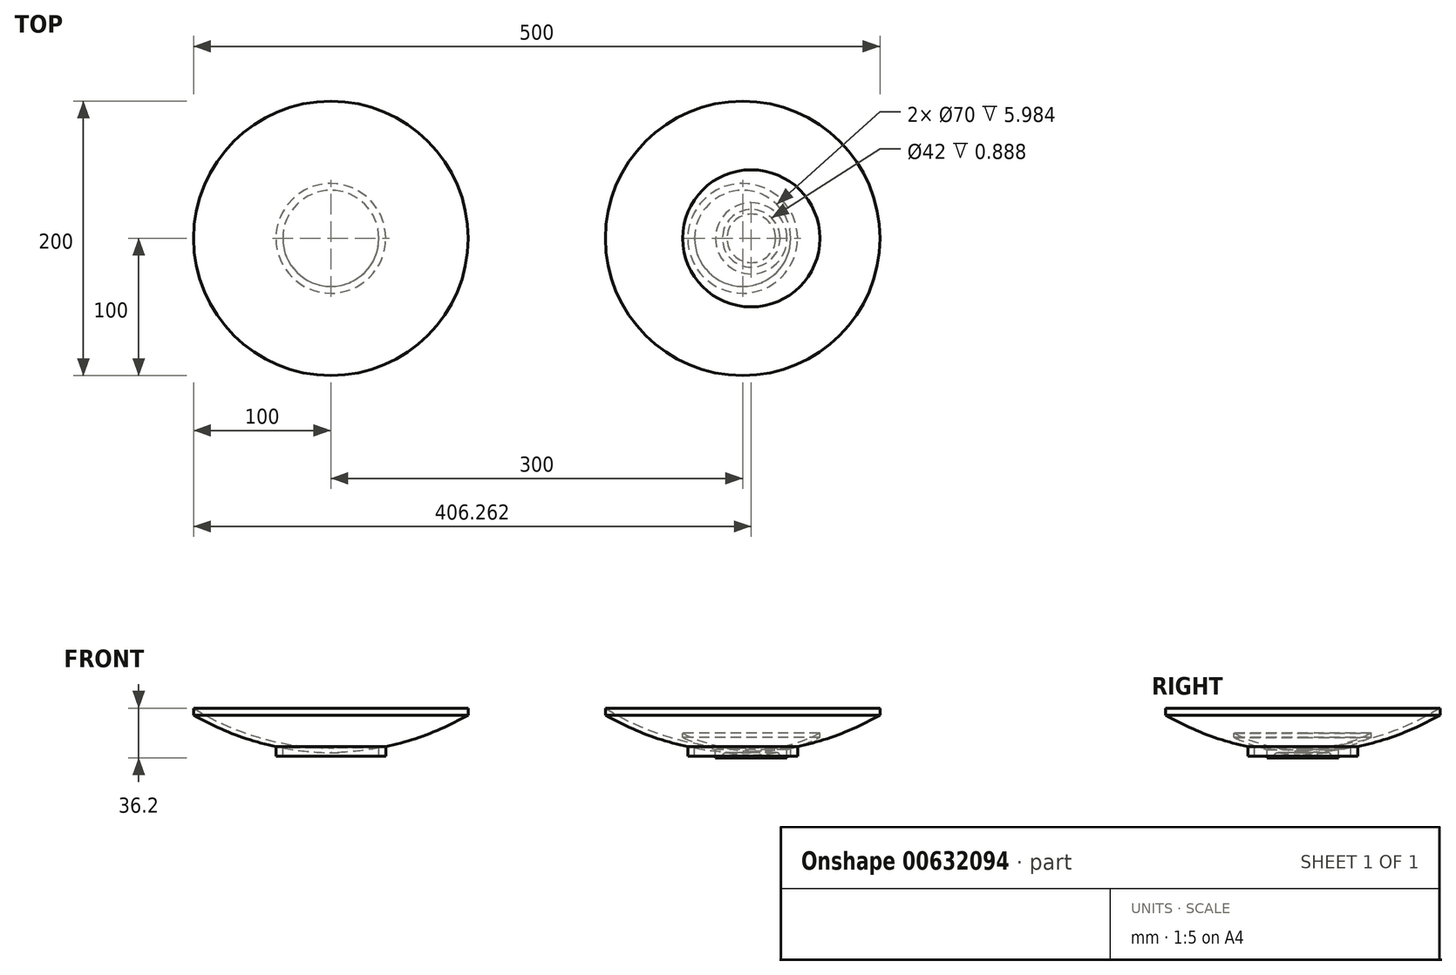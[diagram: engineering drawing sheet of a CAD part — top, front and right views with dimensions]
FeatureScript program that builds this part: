
annotation { "Feature Type Name" : "Feature", "Feature Type Description" : "" }
export const myFeature = defineFeature(function(context is Context, id is Id, definition is map)
    precondition{}
    {
        {
            var Q0;
            Q0=qCreatedBy(makeId("Front.planeOp"),FACE);
            var sketch = newSketch(context, id + "F0", { "sketchPlane" : qUnion([Q0])});
            skLineSegment(sketch, "E0", {"start": v(0, 0) * mm, "end": v(115.16, 0) * mm, "construction": true});
            skLineSegment(sketch, "E1", {"start": v(35, 0) * mm, "end": v(40, 0) * mm});
            skLineSegment(sketch, "E2", {"start": v(40, 0) * mm, "end": v(40, 6.98) * mm});
            skLineSegment(sketch, "E3", {"start": v(35, 0) * mm, "end": v(35, 5.98) * mm});
            skLineSegment(sketch, "E4", {"start": v(100, 35) * mm, "end": v(100, -16.28) * mm, "construction": true});
            skLineSegment(sketch, "E5", {"start": v(0, 5.98) * mm, "end": v(0, 2.5) * mm});
            skLineSegment(sketch, "E6", {"start": v(100, 35) * mm, "end": v(100, 30) * mm});
            skArc(sketch, "E7", {"start": v(0, 5.98) * mm, "mid": v(52.01, 13.55) * mm, "end": v(100, 35) * mm});
            skArc(sketch, "E8", {"start": v(0, 2.5) * mm, "mid": v(51.76, 9.85) * mm, "end": v(100, 30) * mm});
            skSolve(sketch);
        }
        {
            var Q0;
            Q0=makeQuery(id+"F0.imprint","IMPRINT",FACE,{"disambiguationData":[TD([[makeQuery(id+"F0.imprint","IMPRINT",EDGE,{"derivedFrom":sQuery(id+"F0.wireOp",EDGE,"E1")}),1.0]])]});
            var Q1;
            {var subQ2=sQuery(id+"F0.wireOp",EDGE,"E5");Q1=makeQuery(id+"F0.imprint","IMPRINT",FACE,{"disambiguationData":[TD([[makeQuery(id+"F0.imprint","IMPRINT",EDGE,{"derivedFrom":subQ2}),1.0]])]});}
            var Q2;
            Q2=sQuery(id+"F0.wireOp",EDGE,"E5");
            revolve(context, id + "F1", {"entities" : qUnion([Q0, Q1]), "axis" : qUnion([Q2]), "revolveType" : RevolveType.FULL});
        }
        {
            var Q0;
            Q0=makeQuery(id+"F1.opRevolve","SWEPT_BODY",BODY,{"disambiguationData":[OSD([sQuery(id+"F0.wireOp",EDGE,"E1"),sQuery(id+"F0.wireOp",EDGE,"E2"),sQuery(id+"F0.wireOp",EDGE,"E3"),sQuery(id+"F0.wireOp",EDGE,"E5"),sQuery(id+"F0.wireOp",EDGE,"E6"),sQuery(id+"F0.wireOp",EDGE,"E7"),sQuery(id+"F0.wireOp",EDGE,"E8")])]});
            var Q1;
            Q1=sQuery(id+"F0.wireOp",EDGE,"E0");
            transform(context, id + "F2", {"entities" : qUnion([Q0]), "transformType" : TransformType.TRANSLATION_DISTANCE, "transformDirection" : qUnion([Q1]), "distance" : 300 * mm, "makeCopy" : true});
        }
        {
            var Q0;
            Q0=qCreatedBy(makeId("Front.planeOp"),FACE);
            var sketch = newSketch(context, id + "F3", { "sketchPlane" : qUnion([Q0])});
            skLineSegment(sketch, "E9", {"start": v(306.26, -1.2) * mm, "end": v(419.65, -1.2) * mm, "construction": true});
            skLineSegment(sketch, "E10", {"start": v(327.26, -1.2) * mm, "end": v(332.26, -1.2) * mm});
            skLineSegment(sketch, "E11", {"start": v(332.26, -1.2) * mm, "end": v(332.26, 4.79) * mm});
            skLineSegment(sketch, "E12", {"start": v(327.26, -1.2) * mm, "end": v(327.26, -0.31) * mm});
            skLineSegment(sketch, "E13", {"start": v(356.26, 16.8) * mm, "end": v(356.26, -16.28) * mm, "construction": true});
            skLineSegment(sketch, "E14", {"start": v(306.26, 3.57) * mm, "end": v(306.26, 0.72) * mm});
            skLineSegment(sketch, "E15", {"start": v(356.26, 16.8) * mm, "end": v(356.26, 13.8) * mm});
            skLineSegment(sketch, "E16", {"start": v(306.26, 0.72) * mm, "end": v(306.26, -6.73) * mm, "construction": true});
            skFitSpline(sketch, "E17", {"points": [v(306.26, 3.57) * mm, v(331.73, 7.7) * mm, v(356.26, 16.8) * mm], "startDerivative": vector(64.2, 2.57) * mm, "endDerivative": vector(48.25, 25.67) * mm});
            skPoint(sketch, "E18.newPointB", {"position": v(327.26, 3.57) * mm});
            skArc(sketch, "E18.filletArc", {"start": v(327.26, -0.31) * mm, "mid": v(326.27, 1.92) * mm, "end": v(323.96, 2.67) * mm});
            skFitSpline(sketch, "E19", {"points": [v(332.26, 4.79) * mm, v(344.42, 8.65) * mm, v(356.26, 13.8) * mm], "startDerivative": vector(24.28, 6.2) * mm, "endDerivative": vector(23.72, 11.8) * mm});
            skFitSpline(sketch, "E20", {"points": [v(306.26, 0.72) * mm, v(316.48, 1.6) * mm, v(323.96, 2.67) * mm], "startDerivative": vector(20.12, 0.59) * mm, "endDerivative": vector(20, 3.86) * mm});
            skSolve(sketch);
        }
        {
            var Q0;
            {var subQ3=sQuery(id+"F3.wireOp",EDGE,"E14");Q0=makeQuery(id+"F3.imprint","IMPRINT",FACE,{"disambiguationData":[TD([[makeQuery(id+"F3.imprint","IMPRINT",EDGE,{"derivedFrom":subQ3}),1.0]])]});}
            var Q1;
            Q1=makeQuery(id+"F3.imprint","IMPRINT",FACE,{"disambiguationData":[TD([[makeQuery(id+"F3.imprint","IMPRINT",EDGE,{"derivedFrom":sQuery(id+"F3.wireOp",EDGE,"E10")}),1.0]])]});
            var Q2;
            Q2=sQuery(id+"F3.wireOp",EDGE,"E16");
            revolve(context, id + "F4", {"entities" : qUnion([Q0, Q1]), "axis" : qUnion([Q2]), "revolveType" : RevolveType.FULL});
        }
    });
